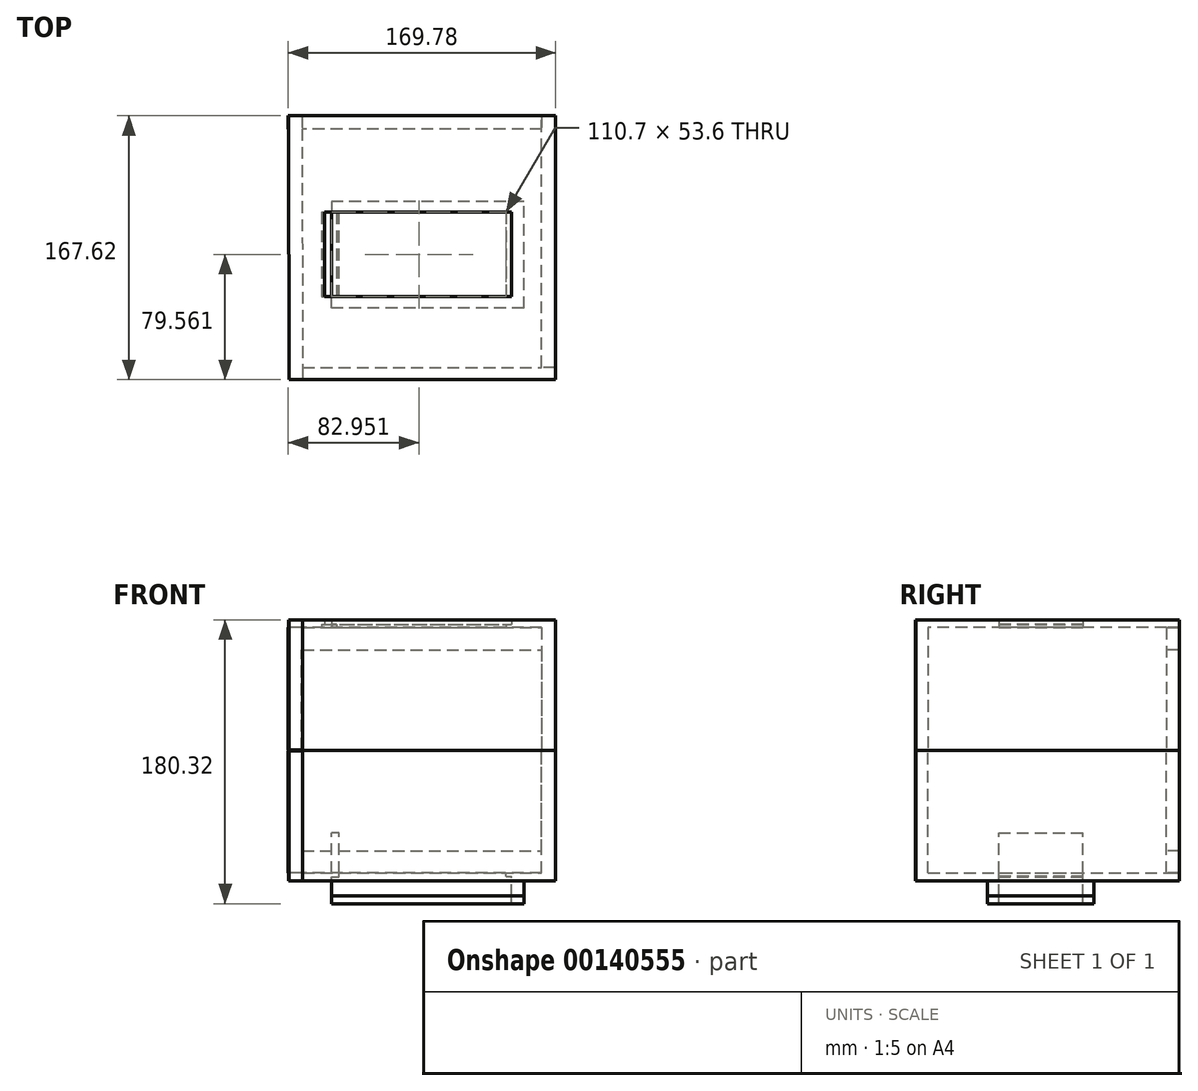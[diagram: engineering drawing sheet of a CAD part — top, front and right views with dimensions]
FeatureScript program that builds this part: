
annotation { "Feature Type Name" : "Feature", "Feature Type Description" : "" }
export const myFeature = defineFeature(function(context is Context, id is Id, definition is map)
    precondition{}
    {
        {
            var Q0;
            Q0=qCreatedBy(makeId("Top.planeOp"),FACE);
            var sketch = newSketch(context, id + "F0", { "sketchPlane" : qUnion([Q0])});
            skLineSegment(sketch, "E0", {"start": v(-75.94, 0) * mm, "end": v(-75.94, -75.61) * mm});
            skLineSegment(sketch, "E1", {"start": v(-75.94, -75.61) * mm, "end": v(76.09, -75.61) * mm});
            skLineSegment(sketch, "E2", {"start": v(76.09, -75.61) * mm, "end": v(76.09, 75.88) * mm});
            skLineSegment(sketch, "E3", {"start": v(76.09, 75.88) * mm, "end": v(-76.12, 75.88) * mm});
            skLineSegment(sketch, "E4", {"start": v(-76.12, 75.88) * mm, "end": v(-75.94, -13.47) * mm});
            skLineSegment(sketch, "E5", {"start": v(-75.94, -13.47) * mm, "end": v(-57.32, -13.47) * mm});
            skLineSegment(sketch, "E6", {"start": v(-57.32, -13.47) * mm, "end": v(-57.32, 59.23) * mm});
            skLineSegment(sketch, "E7", {"start": v(-57.32, 59.23) * mm, "end": v(56.75, 59.23) * mm});
            skLineSegment(sketch, "E8", {"start": v(56.75, 59.23) * mm, "end": v(56.75, -58.96) * mm});
            skLineSegment(sketch, "E9", {"start": v(56.75, -58.96) * mm, "end": v(-57.32, -58.96) * mm});
            skLineSegment(sketch, "E10", {"start": v(-57.32, -58.96) * mm, "end": v(-57.32, -13.47) * mm});
            skSolve(sketch);
        }
        {
            var Q0;
            {var subQ0=sQuery(id+"F0.wireOp",EDGE,"E1");Q0=makeQuery(id+"F0.imprint","IMPRINT",FACE,{"disambiguationData":[TD([[makeQuery(id+"F0.imprint","IMPRINT",EDGE,{"derivedFrom":subQ0}),1.0]])]});}
            extrude(context, id + "F1", {"entities" : qUnion([Q0]), "depth" : 4.96 * mm});
        }
        {
            var Q0;
            Q0=makeQuery(id+"F1.opExtrude","SWEPT_FACE",FACE,{"disambiguationData":[OSD([sQuery(id+"F0.wireOp",EDGE,"E7")])]});
            extrude(context, id + "F2", {"entities" : qUnion([Q0]), "operationType" : NewBodyOperationType.ADD, "depth" : 36.28 * mm});
        }
        {
            var Q0;
            Q0=makeQuery(id+"F1.opExtrude","SWEPT_FACE",FACE,{"disambiguationData":[OSD([sQuery(id+"F0.wireOp",EDGE,"E9")])]});
            extrude(context, id + "F3", {"entities" : qUnion([Q0]), "operationType" : NewBodyOperationType.ADD, "depth" : 28.3 * mm});
        }
        {
            var Q0;
            Q0=makeQuery(id+"F1.opExtrude","SWEPT_FACE",FACE,{"disambiguationData":[OSD([sQuery(id+"F0.wireOp",EDGE,"E2")])]});
            var sketch = newSketch(context, id + "F4", { "sketchPlane" : qUnion([Q0])});
            skLineSegment(sketch, "E11.bottom", {"start": v(-75.61, 4.96) * mm, "end": v(75.88, 4.96) * mm});
            skLineSegment(sketch, "E11.top", {"start": v(-75.61, -78.08) * mm, "end": v(75.88, -78.08) * mm});
            skLineSegment(sketch, "E11.left", {"start": v(-75.61, 4.96) * mm, "end": v(-75.61, -78.08) * mm});
            skLineSegment(sketch, "E11.right", {"start": v(75.88, 4.96) * mm, "end": v(75.88, -78.08) * mm});
            skSolve(sketch);
        }
        {
            var Q0;
            Q0=makeQuery(id+"F1.opExtrude","SWEPT_FACE",FACE,{"disambiguationData":[OSD([sQuery(id+"F0.wireOp",EDGE,"E4")])]});
            var sketch = newSketch(context, id + "F5", { "sketchPlane" : qUnion([Q0])});
            skLineSegment(sketch, "E12.bottom", {"start": v(-76.03, 4.96) * mm, "end": v(75.62, 4.96) * mm});
            skLineSegment(sketch, "E12.top", {"start": v(-76.03, -78.18) * mm, "end": v(75.62, -78.18) * mm});
            skLineSegment(sketch, "E12.left", {"start": v(-76.03, 4.96) * mm, "end": v(-76.03, -78.18) * mm});
            skLineSegment(sketch, "E12.right", {"start": v(75.62, 4.96) * mm, "end": v(75.62, -78.18) * mm});
            skSolve(sketch);
        }
        {
            var Q0;
            Q0=makeQuery(id+"F1.opExtrude","SWEPT_FACE",FACE,{"disambiguationData":[OSD([sQuery(id+"F0.wireOp",EDGE,"E1")])]});
            var sketch = newSketch(context, id + "F6", { "sketchPlane" : qUnion([Q0])});
            skLineSegment(sketch, "E13.bottom", {"start": v(-75.94, 4.96) * mm, "end": v(76.09, 4.96) * mm});
            skLineSegment(sketch, "E13.top", {"start": v(-75.94, -77.97) * mm, "end": v(76.09, -77.97) * mm});
            skLineSegment(sketch, "E13.left", {"start": v(-75.94, 4.96) * mm, "end": v(-75.94, -77.97) * mm});
            skLineSegment(sketch, "E13.right", {"start": v(76.09, 4.96) * mm, "end": v(76.09, -77.97) * mm});
            skSolve(sketch);
        }
        {
            var Q0;
            {var subQ0=sQuery(id+"F6.wireOp",EDGE,"E13.top");Q0=makeQuery(id+"F6.imprint","IMPRINT",FACE,{"disambiguationData":[TD([[makeQuery(id+"F6.imprint","IMPRINT",EDGE,{"derivedFrom":subQ0}),1.0]])]});}
            var Q1;
            {var subQ0=sQuery(id+"F6.wireOp",EDGE,"E13.bottom");Q1=makeQuery(id+"F6.imprint","IMPRINT",FACE,{"disambiguationData":[TD([[makeQuery(id+"F6.imprint","IMPRINT",EDGE,{"derivedFrom":subQ0}),-1.0]])]});}
            extrude(context, id + "F7", {"entities" : qUnion([Q0, Q1]), "operationType" : NewBodyOperationType.ADD, "depth" : 7.7 * mm});
        }
        {
            var Q0;
            {var subQ3=sQuery(id+"F5.wireOp",EDGE,"E12.top");Q0=makeQuery(id+"F5.imprint","IMPRINT",FACE,{"disambiguationData":[TD([[makeQuery(id+"F5.imprint","IMPRINT",EDGE,{"derivedFrom":subQ3}),1.0]])]});}
            var Q1;
            {var subQ3=sQuery(id+"F0.wireOp",EDGE,"E4");var subQ5=makeQuery(id+"F1.opExtrude","CAP_EDGE",EDGE,{"disambiguationData":[OSD([subQ3])],"isStart":true});Q1=makeQuery(id+"F5.imprint","IMPRINT",FACE,{"disambiguationData":[TD([[makeQuery(id+"F5.imprint","IMPRINT",EDGE,{"derivedFrom":subQ5}),1.0]])]});}
            extrude(context, id + "F8", {"entities" : qUnion([Q0, Q1]), "operationType" : NewBodyOperationType.ADD, "depth" : 8.64 * mm});
        }
        {
            var Q0;
            {var subQ0=sQuery(id+"F4.wireOp",EDGE,"E11.top");Q0=makeQuery(id+"F4.imprint","IMPRINT",FACE,{"disambiguationData":[TD([[makeQuery(id+"F4.imprint","IMPRINT",EDGE,{"derivedFrom":subQ0}),1.0]])]});}
            var Q1;
            {var subQ0=sQuery(id+"F4.wireOp",EDGE,"E11.bottom");Q1=makeQuery(id+"F4.imprint","IMPRINT",FACE,{"disambiguationData":[TD([[makeQuery(id+"F4.imprint","IMPRINT",EDGE,{"derivedFrom":subQ0}),-1.0]])]});}
            var Q2;
            Q2=makeQuery(id+"F7.boolean.opBoolean","MERGE",FACE,{"derivedFrom":[makeQuery(id+"F1.opExtrude","SWEPT_FACE",FACE,{"disambiguationData":[OSD([sQuery(id+"F0.wireOp",EDGE,"E2")])]}),makeQuery(id+"F7.opExtrude","SWEPT_FACE",FACE,{"disambiguationData":[OSD([sQuery(id+"F6.wireOp",EDGE,"E13.right")])]})]});
            extrude(context, id + "F9", {"entities" : qUnion([Q0, Q1, Q2]), "operationType" : NewBodyOperationType.ADD, "depth" : 8.77 * mm});
        }
        {
            var Q0;
            Q0=makeQuery(id+"F7.boolean.opBoolean","MERGE",FACE,{"derivedFrom":[makeQuery(id+"F1.opExtrude","SWEPT_FACE",FACE,{"disambiguationData":[OSD([sQuery(id+"F0.wireOp",EDGE,"E0")])]}),makeQuery(id+"F7.opExtrude","SWEPT_FACE",FACE,{"disambiguationData":[OSD([sQuery(id+"F6.wireOp",EDGE,"E13.left")])]})]});
            var sketch = newSketch(context, id + "F10", { "sketchPlane" : qUnion([Q0])});
            skSolve(sketch);
        }
        {
            var Q0;
            Q0=qSketchRegion(id+"F10",true);
            var Q1;
            Q1=makeQuery(id+"F8.opExtrude","SWEPT_FACE",FACE,{"disambiguationData":[OSD([sQuery(id+"F5.wireOp",EDGE,"E12.right")])]});
            extrude(context, id + "F11", {"entities" : qUnion([Q0, Q1]), "operationType" : NewBodyOperationType.ADD, "depth" : 7.64 * mm});
        }
        {
            var Q0;
            Q0=makeQuery(id+"F9.boolean.opBoolean","MERGE",FACE,{"derivedFrom":[makeQuery(id+"F1.opExtrude","SWEPT_FACE",FACE,{"disambiguationData":[OSD([sQuery(id+"F0.wireOp",EDGE,"E3")])]}),makeQuery(id+"F9.opExtrude","SWEPT_FACE",FACE,{"disambiguationData":[OSD([sQuery(id+"F4.wireOp",EDGE,"E11.right")])]})]});
            var sketch = newSketch(context, id + "F12", { "sketchPlane" : qUnion([Q0])});
            skFitSpline(sketch, "E14", {"points": [v(-76.09, -78.08) * mm, v(0, -14.04) * mm, v(76.51, -78.08) * mm], "startDerivative": vector(152.15, 192.16) * mm, "endDerivative": vector(153.05, -192.05) * mm});
            skSolve(sketch);
        }
        {
            var Q0;
            {var subQ1=sQuery(id+"F0.wireOp",EDGE,"E3");Q0=makeQuery(id+"F12.imprint","IMPRINT",FACE,{"disambiguationData":[TD([[makeQuery(id+"F12.imprint","IMPRINT",EDGE,{"derivedFrom":makeQuery(id+"F1.opExtrude","CAP_EDGE",EDGE,{"disambiguationData":[OSD([subQ1])],"isStart":true})}),1.0]])]});}
            var sketch = newSketch(context, id + "F13", { "sketchPlane" : qUnion([Q0])});
            skLineSegment(sketch, "E15", {"start": v(0, 0) * mm, "end": v(84.92, 0) * mm});
            skLineSegment(sketch, "E16", {"start": v(84.92, 0) * mm, "end": v(84.92, -77.55) * mm});
            skLineSegment(sketch, "E17", {"start": v(84.92, -77.55) * mm, "end": v(76.3, -77.55) * mm});
            skLineSegment(sketch, "E18", {"start": v(76.3, -77.55) * mm, "end": v(76.3, -14.05) * mm});
            skLineSegment(sketch, "E19", {"start": v(76.3, -14.05) * mm, "end": v(-76.33, -14.05) * mm});
            skLineSegment(sketch, "E20", {"start": v(-76.33, -14.05) * mm, "end": v(-76.33, -77.57) * mm});
            skLineSegment(sketch, "E21", {"start": v(-76.33, -77.57) * mm, "end": v(-85.18, -77.57) * mm});
            skLineSegment(sketch, "E22", {"start": v(-85.18, -77.57) * mm, "end": v(-85.18, 0) * mm});
            skLineSegment(sketch, "E23", {"start": v(-85.18, 0) * mm, "end": v(0, 0) * mm});
            skSolve(sketch);
        }
        {
            var Q0;
            {var subQ1=sQuery(id+"F0.wireOp",EDGE,"E3");Q0=makeQuery(id+"F12.imprint","IMPRINT",FACE,{"disambiguationData":[TD([[makeQuery(id+"F12.imprint","IMPRINT",EDGE,{"derivedFrom":makeQuery(id+"F1.opExtrude","CAP_EDGE",EDGE,{"disambiguationData":[OSD([subQ1])],"isStart":true})}),1.0]])]});}
            var Q1;
            {var subQ0=sQuery(id+"F13.wireOp",EDGE,"E16");Q1=makeQuery(id+"F13.imprint","IMPRINT",FACE,{"disambiguationData":[TD([[makeQuery(id+"F13.imprint","IMPRINT",EDGE,{"derivedFrom":subQ0}),-1.0]])]});}
            var Q2;
            Q2=makeQuery(id+"F8.opExtrude","SWEPT_FACE",FACE,{"disambiguationData":[OSD([sQuery(id+"F5.wireOp",EDGE,"E12.left")])]});
            extrude(context, id + "F14", {"entities" : qUnion([Q0, Q1, Q2]), "operationType" : NewBodyOperationType.ADD, "depth" : 8.32 * mm});
        }
        {
            var Q0;
            {var subQ0=sQuery(id+"F0.wireOp",EDGE,"E9");var subQ1=sQuery(id+"F0.wireOp",EDGE,"E7");Q0=makeQuery(id+"F3.boolean.opBoolean","MERGE",FACE,{"derivedFrom":[makeQuery(id+"F2.boolean.opBoolean","MERGE",FACE,{"derivedFrom":[makeQuery(id+"F1.opExtrude","CAP_FACE",FACE,{"disambiguationData":[OSD([sQuery(id+"F0.wireOp",EDGE,"E0"),sQuery(id+"F0.wireOp",EDGE,"E1"),sQuery(id+"F0.wireOp",EDGE,"E2"),sQuery(id+"F0.wireOp",EDGE,"E3"),sQuery(id+"F0.wireOp",EDGE,"E4"),sQuery(id+"F0.wireOp",EDGE,"E6"),subQ1,sQuery(id+"F0.wireOp",EDGE,"E8"),subQ0,sQuery(id+"F0.wireOp",EDGE,"E10")])],"isStart":true}),makeQuery(id+"F2.opExtrude","SWEPT_FACE",FACE,{"disambiguationData":[OSD([subQ1]),TDD([makeQuery(id+"F1.opExtrude","CAP_EDGE",EDGE,{"disambiguationData":[OSD([subQ1])],"isStart":true})])]})]}),makeQuery(id+"F3.opExtrude","SWEPT_FACE",FACE,{"disambiguationData":[OSD([subQ0]),TDD([makeQuery(id+"F1.opExtrude","CAP_EDGE",EDGE,{"disambiguationData":[OSD([subQ0])],"isStart":true})])]})]});}
            var sketch = newSketch(context, id + "F15", { "sketchPlane" : qUnion([Q0])});
            skLineSegment(sketch, "E24", {"start": v(56.75, -22.94) * mm, "end": v(53.38, -22.94) * mm});
            skLineSegment(sketch, "E25", {"start": v(53.38, -22.94) * mm, "end": v(53.38, 30.66) * mm});
            skLineSegment(sketch, "E26", {"start": v(53.38, 30.66) * mm, "end": v(56.75, 30.66) * mm});
            skLineSegment(sketch, "E27", {"start": v(56.75, 30.66) * mm, "end": v(56.75, -22.94) * mm});
            skSolve(sketch);
        }
        {
            var Q0;
            {var subQ7=sQuery(id+"F15.wireOp",EDGE,"E24");Q0=makeQuery(id+"F15.imprint","IMPRINT",FACE,{"disambiguationData":[TD([[makeQuery(id+"F15.imprint","IMPRINT",EDGE,{"derivedFrom":subQ7}),-1.0]])]});}
            var sketch = newSketch(context, id + "F16", { "sketchPlane" : qUnion([Q0])});
            skLineSegment(sketch, "E28", {"start": v(-57.09, 30.4) * mm, "end": v(-57.09, -22.82) * mm});
            skLineSegment(sketch, "E29", {"start": v(-57.09, -22.82) * mm, "end": v(-54.16, -22.82) * mm});
            skLineSegment(sketch, "E30", {"start": v(-54.16, -22.82) * mm, "end": v(-54.16, 30.4) * mm});
            skLineSegment(sketch, "E31", {"start": v(-54.16, 30.4) * mm, "end": v(-57.09, 30.4) * mm});
            skSolve(sketch);
        }
        {
            var Q0;
            Q0=makeQuery(id+"F16.imprint","IMPRINT",FACE,{"disambiguationData":[TD([[makeQuery(id+"F16.imprint","IMPRINT",EDGE,{"derivedFrom":sQuery(id+"F16.wireOp",EDGE,"E28")}),1.0]])]});
            var Q1;
            Q1=makeQuery(id+"F15.imprint","IMPRINT",FACE,{"disambiguationData":[TD([[makeQuery(id+"F15.imprint","IMPRINT",EDGE,{"derivedFrom":sQuery(id+"F15.wireOp",EDGE,"E24")}),1.0]])]});
            extrude(context, id + "F17", {"entities" : qUnion([Q0, Q1]), "operationType" : NewBodyOperationType.ADD, "oppositeDirection" : true, "depth" : 2.05 * mm});
        }
        {
            var Q0;
            Q0=makeQuery(id+"F1.opExtrude","SWEPT_BODY",BODY,{"disambiguationData":[OSD([sQuery(id+"F0.wireOp",EDGE,"E0"),sQuery(id+"F0.wireOp",EDGE,"E1"),sQuery(id+"F0.wireOp",EDGE,"E2"),sQuery(id+"F0.wireOp",EDGE,"E3"),sQuery(id+"F0.wireOp",EDGE,"E4"),sQuery(id+"F0.wireOp",EDGE,"E6"),sQuery(id+"F0.wireOp",EDGE,"E7"),sQuery(id+"F0.wireOp",EDGE,"E8"),sQuery(id+"F0.wireOp",EDGE,"E9"),sQuery(id+"F0.wireOp",EDGE,"E10")])]});
            var Q1;
            {var subQ0=sQuery(id+"F6.wireOp",EDGE,"E13.top");Q1=makeQuery(id+"F9.boolean.opBoolean","MERGE",FACE,{"derivedFrom":[makeQuery(id+"F7.opExtrude","SWEPT_FACE",FACE,{"disambiguationData":[OSD([subQ0])]}),makeQuery(id+"F9.opExtrude","SWEPT_FACE",FACE,{"disambiguationData":[OSD([subQ0,sQuery(id+"F6.wireOp",EDGE,"E13.right")])]})]});}
            mirror(context, id + "F18", {"operationType" : NewBodyOperationType.ADD, "entities" : qUnion([Q0]), "mirrorPlane" : qUnion([Q1])});
        }
        {
            var Q0;
            Q0=makeQuery(id+"F17.opExtrude","SWEPT_FACE",FACE,{"disambiguationData":[OSD([sQuery(id+"F15.wireOp",EDGE,"E25")])]});
            extrude(context, id + "F19", {"entities" : qUnion([Q0]), "depth" : 117.2 * mm});
        }
        {
            var Q0;
            Q0=makeQuery(id+"F1.opExtrude","SWEPT_FACE",FACE,{"disambiguationData":[OSD([sQuery(id+"F0.wireOp",EDGE,"E8")])]});
            extrude(context, id + "F20", {"entities" : qUnion([Q0]), "depth" : 118.63 * mm});
        }
        {
            var Q0;
            {var subQ0=sQuery(id+"F4.wireOp",EDGE,"E11.bottom");var subQ1=sQuery(id+"F0.wireOp",EDGE,"E3");var subQ2=sQuery(id+"F5.wireOp",EDGE,"E12.bottom");var subQ3=sQuery(id+"F6.wireOp",EDGE,"E13.bottom");var subQ4=sQuery(id+"F0.wireOp",EDGE,"E2");var subQ5=sQuery(id+"F0.wireOp",EDGE,"E9");var subQ6=sQuery(id+"F0.wireOp",EDGE,"E7");Q0=makeQuery(id+"F18.opPattern","COPY",FACE,{"derivedFrom":makeQuery(id+"F14.boolean.opBoolean","MERGE",FACE,{"derivedFrom":[makeQuery(id+"F11.boolean.opBoolean","MERGE",FACE,{"derivedFrom":[makeQuery(id+"F9.boolean.opBoolean","MERGE",FACE,{"derivedFrom":[makeQuery(id+"F8.boolean.opBoolean","MERGE",FACE,{"derivedFrom":[makeQuery(id+"F7.boolean.opBoolean","MERGE",FACE,{"derivedFrom":[makeQuery(id+"F3.boolean.opBoolean","MERGE",FACE,{"derivedFrom":[makeQuery(id+"F2.boolean.opBoolean","MERGE",FACE,{"derivedFrom":[makeQuery(id+"F1.opExtrude","CAP_FACE",FACE,{"disambiguationData":[OSD([sQuery(id+"F0.wireOp",EDGE,"E0"),sQuery(id+"F0.wireOp",EDGE,"E1"),subQ4,subQ1,sQuery(id+"F0.wireOp",EDGE,"E4"),sQuery(id+"F0.wireOp",EDGE,"E6"),subQ6,sQuery(id+"F0.wireOp",EDGE,"E8"),subQ5,sQuery(id+"F0.wireOp",EDGE,"E10")])],"isStart":false}),makeQuery(id+"F2.opExtrude","SWEPT_FACE",FACE,{"disambiguationData":[OSD([subQ6]),TDD([makeQuery(id+"F1.opExtrude","CAP_EDGE",EDGE,{"disambiguationData":[OSD([subQ6])],"isStart":false})])]})]}),makeQuery(id+"F3.opExtrude","SWEPT_FACE",FACE,{"disambiguationData":[OSD([subQ5]),TDD([makeQuery(id+"F1.opExtrude","CAP_EDGE",EDGE,{"disambiguationData":[OSD([subQ5])],"isStart":false})])]})]}),makeQuery(id+"F7.opExtrude","SWEPT_FACE",FACE,{"disambiguationData":[OSD([subQ3])]})]}),makeQuery(id+"F8.opExtrude","SWEPT_FACE",FACE,{"disambiguationData":[OSD([subQ2])]})]}),makeQuery(id+"F9.opExtrude","SWEPT_FACE",FACE,{"disambiguationData":[OSD([subQ0])]}),makeQuery(id+"F9.opExtrude","SWEPT_FACE",FACE,{"disambiguationData":[OSD([subQ4,subQ3,sQuery(id+"F6.wireOp",EDGE,"E13.right")])]})]}),makeQuery(id+"F11.opExtrude","SWEPT_FACE",FACE,{"disambiguationData":[OSD([subQ2,sQuery(id+"F5.wireOp",EDGE,"E12.right")])]})]}),makeQuery(id+"F14.opExtrude","SWEPT_FACE",FACE,{"disambiguationData":[OSD([subQ2,sQuery(id+"F5.wireOp",EDGE,"E12.left")])]}),makeQuery(id+"F14.opExtrude","SWEPT_FACE",FACE,{"disambiguationData":[OSD([subQ1,subQ0,sQuery(id+"F4.wireOp",EDGE,"E11.right")])]})]}),"instanceName":"1"});}
            var sketch = newSketch(context, id + "F21", { "sketchPlane" : qUnion([Q0])});
            skLineSegment(sketch, "E32", {"start": v(56.75, 30.66) * mm, "end": v(56.75, 37.97) * mm});
            skLineSegment(sketch, "E33", {"start": v(56.75, 37.97) * mm, "end": v(-57.27, 37.97) * mm});
            skLineSegment(sketch, "E34", {"start": v(-57.27, 37.97) * mm, "end": v(-57.32, 30.66) * mm});
            skLineSegment(sketch, "E35", {"start": v(-57.32, 30.66) * mm, "end": v(56.75, 30.66) * mm});
            skLineSegment(sketch, "E36", {"start": v(56.75, 37.97) * mm, "end": v(64.86, 37.97) * mm});
            skLineSegment(sketch, "E37", {"start": v(64.86, 37.97) * mm, "end": v(64.86, -29.79) * mm});
            skLineSegment(sketch, "E38", {"start": v(64.86, -29.79) * mm, "end": v(-57.32, -29.79) * mm});
            skLineSegment(sketch, "E39", {"start": v(-57.32, -29.79) * mm, "end": v(-57.32, -22.94) * mm});
            skLineSegment(sketch, "E40", {"start": v(-57.32, -22.94) * mm, "end": v(56.75, -22.94) * mm});
            skLineSegment(sketch, "E41", {"start": v(56.75, -22.94) * mm, "end": v(56.75, 30.66) * mm});
            skSolve(sketch);
        }
        {
            var Q0;
            Q0=makeQuery(id+"F21.imprint","IMPRINT",FACE,{"disambiguationData":[TD([[makeQuery(id+"F21.imprint","IMPRINT",EDGE,{"derivedFrom":sQuery(id+"F21.wireOp",EDGE,"E32")}),1.0]])]});
            var Q1;
            Q1=makeQuery(id+"F21.imprint","IMPRINT",FACE,{"disambiguationData":[TD([[makeQuery(id+"F21.imprint","IMPRINT",EDGE,{"derivedFrom":sQuery(id+"F21.wireOp",EDGE,"E32")}),-1.0]])]});
            extrude(context, id + "F22", {"entities" : qUnion([Q0, Q1]), "operationType" : NewBodyOperationType.ADD, "depth" : 9.64 * mm});
        }
        {
            var Q0;
            Q0=makeQuery(id+"F22.opExtrude","CAP_FACE",FACE,{"disambiguationData":[OSD([sQuery(id+"F21.wireOp",EDGE,"E33"),sQuery(id+"F21.wireOp",EDGE,"E34"),sQuery(id+"F21.wireOp",EDGE,"E35"),sQuery(id+"F21.wireOp",EDGE,"E36"),sQuery(id+"F21.wireOp",EDGE,"E37"),sQuery(id+"F21.wireOp",EDGE,"E38"),sQuery(id+"F21.wireOp",EDGE,"E39"),sQuery(id+"F21.wireOp",EDGE,"E40"),sQuery(id+"F21.wireOp",EDGE,"E41")])],"isStart":false});
            var sketch = newSketch(context, id + "F23", { "sketchPlane" : qUnion([Q0])});
            skLineSegment(sketch, "E42", {"start": v(-57.32, 30.66) * mm, "end": v(-57.32, -22.94) * mm});
            skLineSegment(sketch, "E43", {"start": v(-57.32, -22.94) * mm, "end": v(56.75, -22.94) * mm});
            skLineSegment(sketch, "E44", {"start": v(56.75, -22.94) * mm, "end": v(56.75, 30.66) * mm});
            skLineSegment(sketch, "E45", {"start": v(56.75, 30.66) * mm, "end": v(-57.32, 30.66) * mm});
            skSolve(sketch);
        }
        {
            var Q0;
            Q0=makeQuery(id+"F23.imprint","IMPRINT",FACE,{"disambiguationData":[TD([[makeQuery(id+"F23.imprint","IMPRINT",EDGE,{"derivedFrom":sQuery(id+"F23.wireOp",EDGE,"E42")}),1.0]])]});
            extrude(context, id + "F24", {"entities" : qUnion([Q0]), "depth" : 4.83 * mm});
        }
        {
            var Q0;
            Q0=makeQuery(id+"F22.opExtrude","CAP_FACE",FACE,{"disambiguationData":[OSD([sQuery(id+"F21.wireOp",EDGE,"E33"),sQuery(id+"F21.wireOp",EDGE,"E34"),sQuery(id+"F21.wireOp",EDGE,"E35"),sQuery(id+"F21.wireOp",EDGE,"E36"),sQuery(id+"F21.wireOp",EDGE,"E37"),sQuery(id+"F21.wireOp",EDGE,"E38"),sQuery(id+"F21.wireOp",EDGE,"E39"),sQuery(id+"F21.wireOp",EDGE,"E40"),sQuery(id+"F21.wireOp",EDGE,"E41")])],"isStart":false});
            extrude(context, id + "F25", {"entities" : qUnion([Q0]), "depth" : 4.8 * mm});
        }
        {
            var Q0;
            {var subQ0=sQuery(id+"F0.wireOp",EDGE,"E9");var subQ1=sQuery(id+"F0.wireOp",EDGE,"E7");Q0=makeQuery(id+"F18.opPattern","COPY",FACE,{"derivedFrom":makeQuery(id+"F17.boolean.opBoolean","MERGE",FACE,{"derivedFrom":[makeQuery(id+"F3.boolean.opBoolean","MERGE",FACE,{"derivedFrom":[makeQuery(id+"F2.boolean.opBoolean","MERGE",FACE,{"derivedFrom":[makeQuery(id+"F1.opExtrude","CAP_FACE",FACE,{"disambiguationData":[OSD([sQuery(id+"F0.wireOp",EDGE,"E0"),sQuery(id+"F0.wireOp",EDGE,"E1"),sQuery(id+"F0.wireOp",EDGE,"E2"),sQuery(id+"F0.wireOp",EDGE,"E3"),sQuery(id+"F0.wireOp",EDGE,"E4"),sQuery(id+"F0.wireOp",EDGE,"E6"),subQ1,sQuery(id+"F0.wireOp",EDGE,"E8"),subQ0,sQuery(id+"F0.wireOp",EDGE,"E10")])],"isStart":true}),makeQuery(id+"F2.opExtrude","SWEPT_FACE",FACE,{"disambiguationData":[OSD([subQ1]),TDD([makeQuery(id+"F1.opExtrude","CAP_EDGE",EDGE,{"disambiguationData":[OSD([subQ1])],"isStart":true})])]})]}),makeQuery(id+"F3.opExtrude","SWEPT_FACE",FACE,{"disambiguationData":[OSD([subQ0]),TDD([makeQuery(id+"F1.opExtrude","CAP_EDGE",EDGE,{"disambiguationData":[OSD([subQ0])],"isStart":true})])]})]}),makeQuery(id+"F17.opExtrude","CAP_FACE",FACE,{"disambiguationData":[OSD([sQuery(id+"F15.wireOp",EDGE,"E24"),sQuery(id+"F15.wireOp",EDGE,"E25"),sQuery(id+"F15.wireOp",EDGE,"E26"),sQuery(id+"F15.wireOp",EDGE,"E27")])],"isStart":true})]}),"instanceName":"1"});}
            var sketch = newSketch(context, id + "F26", { "sketchPlane" : qUnion([Q0])});
            skLineSegment(sketch, "E46", {"start": v(-57.32, 22.94) * mm, "end": v(-57.32, -30.66) * mm});
            skLineSegment(sketch, "E47", {"start": v(-57.32, -30.66) * mm, "end": v(-52.54, -30.66) * mm});
            skLineSegment(sketch, "E48", {"start": v(-52.54, -30.66) * mm, "end": v(-52.54, 22.94) * mm});
            skLineSegment(sketch, "E49", {"start": v(-52.54, 22.94) * mm, "end": v(-57.32, 22.94) * mm});
            skSolve(sketch);
        }
        {
            var Q0;
            Q0=makeQuery(id+"F26.imprint","IMPRINT",FACE,{"disambiguationData":[TD([[makeQuery(id+"F26.imprint","IMPRINT",EDGE,{"derivedFrom":sQuery(id+"F26.wireOp",EDGE,"E46")}),-1.0]])]});
            extrude(context, id + "F27", {"entities" : qUnion([Q0]), "operationType" : NewBodyOperationType.ADD, "oppositeDirection" : true, "depth" : 2.5 * mm, "hasSecondDirection" : true, "secondDirectionOppositeDirection" : false, "secondDirectionDepth" : 25.4 * mm});
        }
    });
